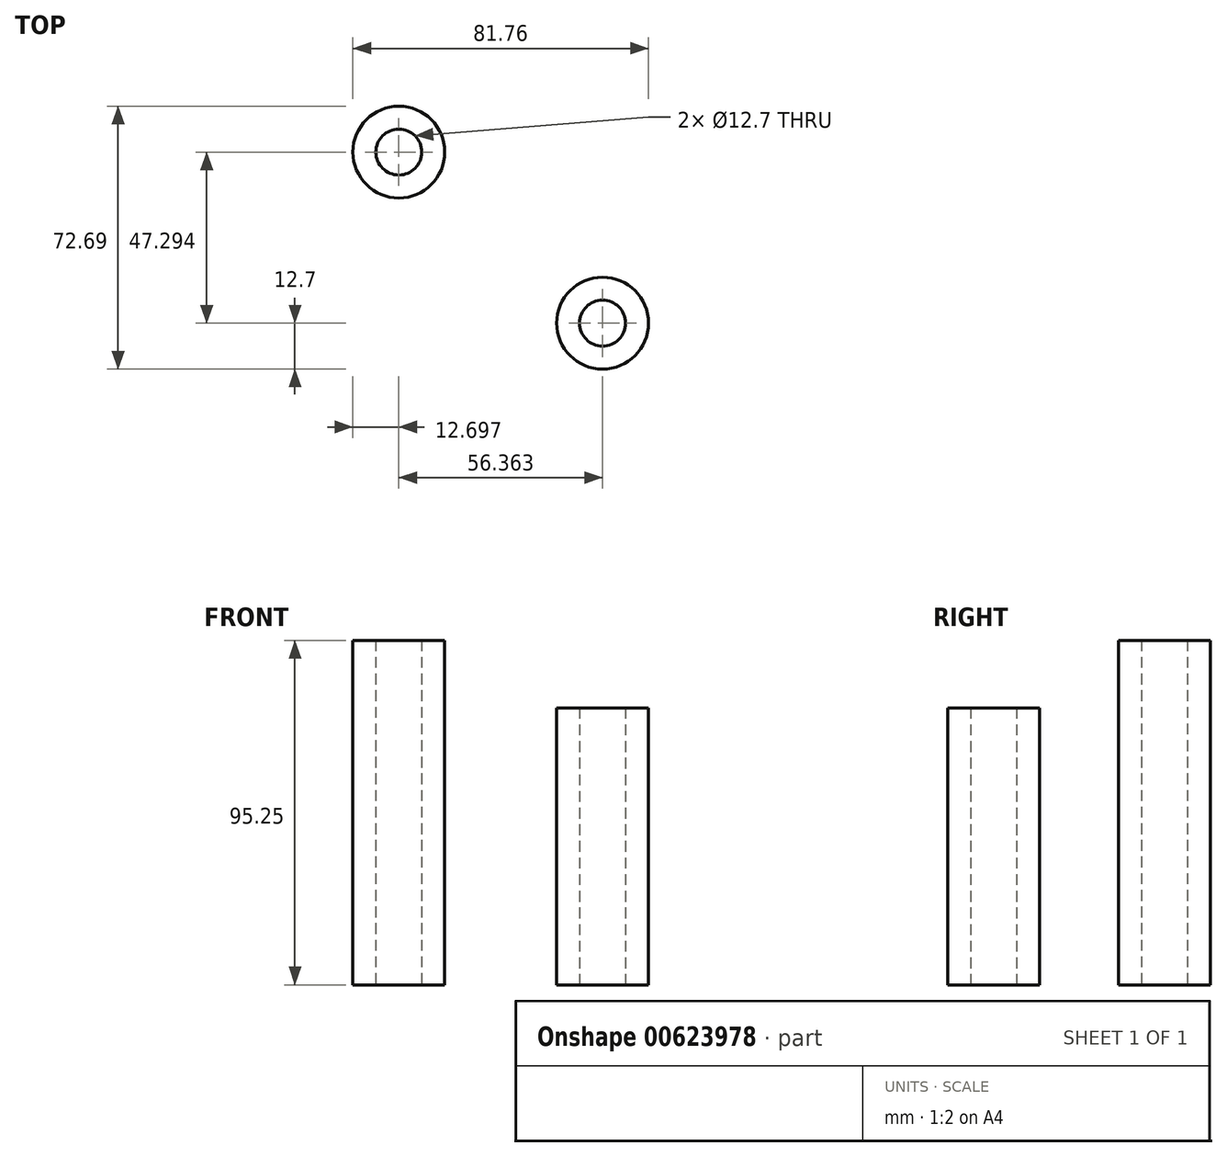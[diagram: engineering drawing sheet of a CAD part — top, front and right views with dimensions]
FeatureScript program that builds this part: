
annotation { "Feature Type Name" : "Feature", "Feature Type Description" : "" }
export const myFeature = defineFeature(function(context is Context, id is Id, definition is map)
    precondition{}
    {
        {
            var Q0;
            Q0=qCreatedBy(makeId("Top.planeOp"),FACE);
            var sketch = newSketch(context, id + "F0", { "sketchPlane" : qUnion([Q0])});
            skCircle(sketch, "E0", {"center": v(0, 0) * mm, "radius": 12.7 * mm});
            skCircle(sketch, "E1", {"center": v(0, 0) * mm, "radius": 6.35 * mm});
            skCircle(sketch, "E2", {"center": v(-56.36, 47.3) * mm, "radius": 12.7 * mm});
            skCircle(sketch, "E3", {"center": v(-56.36, 47.3) * mm, "radius": 6.35 * mm});
            skSolve(sketch);
        }
        {
            var Q0;
            Q0=makeQuery(id+"F0.imprint","IMPRINT",FACE,{"disambiguationData":[TD([[makeQuery(id+"F0.imprint","IMPRINT",EDGE,{"derivedFrom":sQuery(id+"F0.wireOp",EDGE,"E2")}),1.0]])]});
            extrude(context, id + "F1", {"entities" : qUnion([Q0]), "depth" : 95.25 * mm, "offsetDistance" : 25.4 * mm});
        }
        {
            var Q0;
            Q0=makeQuery(id+"F0.imprint","IMPRINT",FACE,{"disambiguationData":[TD([[makeQuery(id+"F0.imprint","IMPRINT",EDGE,{"derivedFrom":sQuery(id+"F0.wireOp",EDGE,"E0")}),1.0]])]});
            extrude(context, id + "F2", {"entities" : qUnion([Q0]), "depth" : 31.75 * mm, "offsetDistance" : 25.4 * mm});
        }
        {
            var Q0;
            Q0=makeQuery(id+"F2.opExtrude","CAP_FACE",FACE,{"disambiguationData":[OSD([sQuery(id+"F0.wireOp",EDGE,"E0"),sQuery(id+"F0.wireOp",EDGE,"E1")])],"isStart":false});
            extrude(context, id + "F3", {"entities" : qUnion([Q0]), "operationType" : NewBodyOperationType.ADD, "depth" : 44.83 * mm, "offsetDistance" : 25.4 * mm});
        }
    });
